# Revit family: IEK_РозеткаСетевая_Встраиваемая_С ЗК ЗШ и Кр16А одноместная IP44_КВАРТА
name_source: partatom
category: Электрические приборы
units: mm (PartAtom-declared; Revit-internal decimal feet)

## family parameters
Всегда вертикально = Да
На основе рабочей плоскости = Нет
Общий = Нет
При загрузке вырезать с полостями = Нет
Размер круглого соединителя = Использовать диаметр
Сохранять ориентацию аннотаций = Да
Тип детали = Нормальный
Точка расчета площади = Нет

## types (2) — shared parameters
ADSK_Версия Revit = 2019
ADSK_Версия семейства = 1.0
ADSK_Группирование = III ЭЛЕКТРОУСТАНОВОЧНЫЕ И ЭЛЕКТРОМОНТАЖНЫЕ ИЗДЕЛИЯ
ADSK_Единица измерения = шт
ADSK_Завод-изготовитель = IEK
ADSK_Количество фаз = 1
ADSK_Количество фаз числовое = 1
ADSK_Марка = КВАРТА
ADSK_Материал = Цвет белый
ADSK_Материал наименование = Пластик
ADSK_Напряжение = 220 В
IEK_URL = https://www.iek.ru
IEK_Описание = Классический дизайн, проверенный временем и востребованный различными категориями потребителей, позволяет устанавливать изделия серии "КВАРТА" в квартирах, загородных домах, офисных и производственных помещениях.
KSI_CMa_Строительные материалы = 01.7.14.03
KSI_CPr_Строительные изделия = 20.4.03.04 20.4.03.05 20.4.03.06
Высота = 81 мм
Глубина = 68 мм
Изготовитель = IEK
Степень защиты = IP44
Тип монтажа = Скрытый монтаж (в штукатурку)
Ширина = 82 мм

## per-type parameters (varying)
| type | ADSK_URL страницы изделия | ADSK_Код изделия | ADSK_Масса | ADSK_Наименование | IEK_Цена за единицу |
| РСбш10-3-ККБ-44 |  | ERK70-K01-10-DM-44 | 0.13 | Розетка 1-местная РСбш10-3-ККБ-44 с заземляющим контактом с защитной шторкой с крышкой керамика IP44 16А КВАРТА белый IEK | 237.44 |
| РСбш11-3-ККБ-44 | https://www.iek.ru | ERK71-K01-10-DM-44 | 0.135 | Розетка 1-местная РСбш11-3-ККБ-44 с заземляющим контактом с защитной шторкой с бол. кр. керамика IP44 16А КВАРТА белый IEK | 268.64 |
